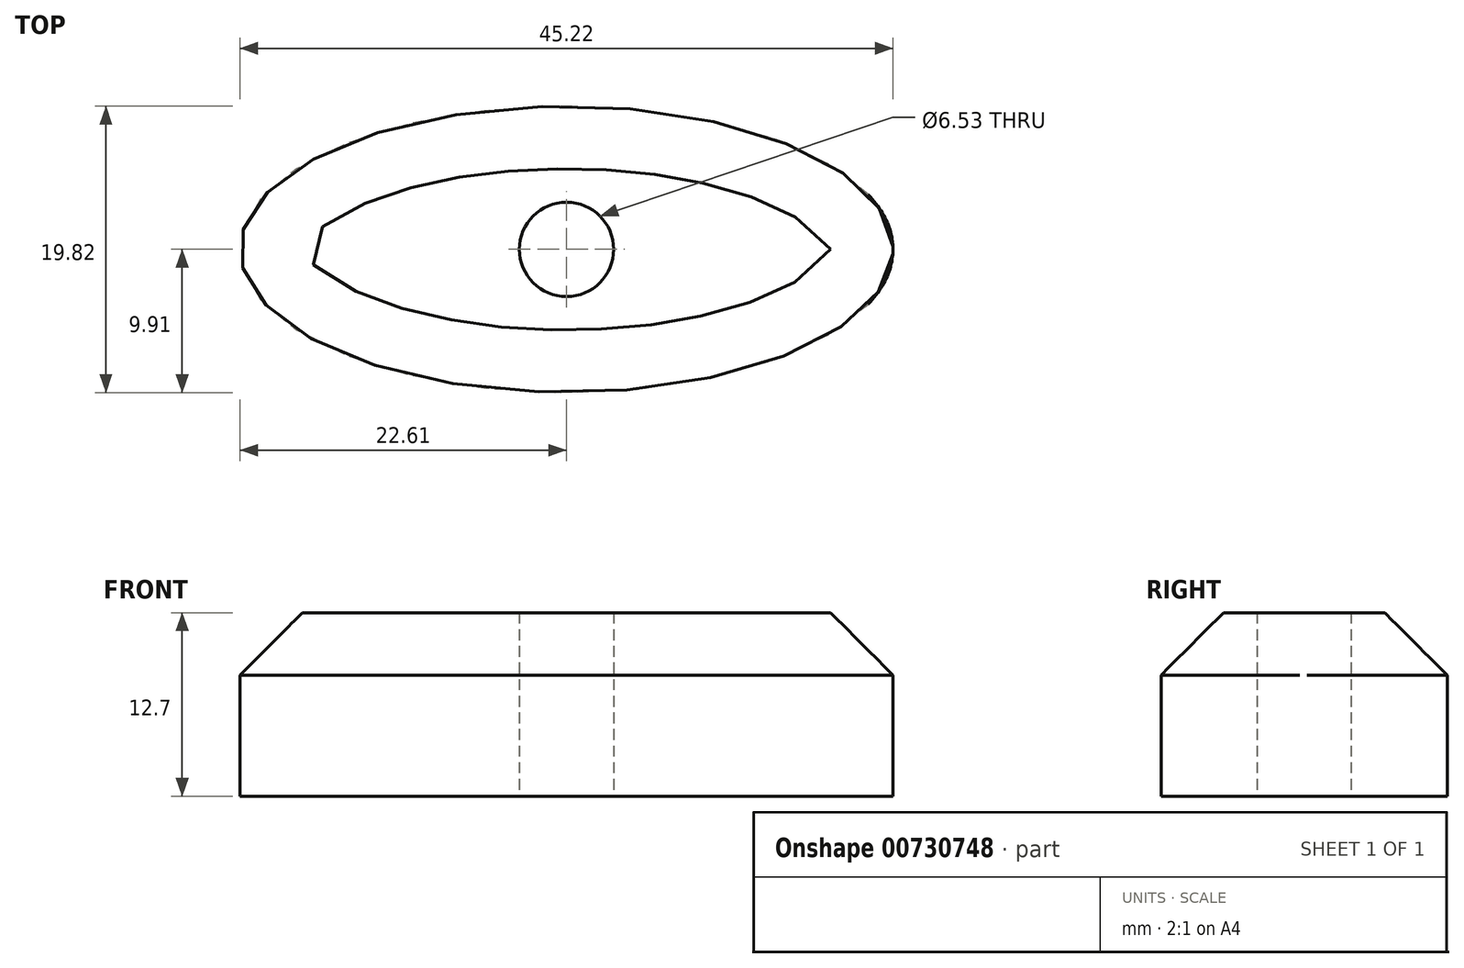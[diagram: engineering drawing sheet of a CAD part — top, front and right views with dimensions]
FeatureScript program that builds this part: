
annotation { "Feature Type Name" : "Feature", "Feature Type Description" : "" }
export const myFeature = defineFeature(function(context is Context, id is Id, definition is map)
    precondition{}
    {
        {
            var Q0;
            Q0=qCreatedBy(makeId("Top.planeOp"),FACE);
            var sketch = newSketch(context, id + "F0", { "sketchPlane" : qUnion([Q0])});
            skEllipse(sketch, "E0", {"center": v(0, 0) * mm, "majorRadius": 22.6 * mm, "minorRadius": 9.9 * mm, "majorAxis": v(1, 0)});
            skSolve(sketch);
        }
        {
            var Q0;
            Q0=makeQuery(id+"F0.imprint","IMPRINT",FACE,{"disambiguationData":[TD([[makeQuery(id+"F0.imprint","IMPRINT",EDGE,{"derivedFrom":sQuery(id+"F0.wireOp",EDGE,"E0")}),1.0]])]});
            extrude(context, id + "F1", {"entities" : qUnion([Q0]), "depth" : 12.7 * mm, "offsetDistance" : 25.4 * mm});
        }
        {
            var Q0;
            Q0=makeQuery(id+"F1.opExtrude","CAP_EDGE",EDGE,{"disambiguationData":[OSD([sQuery(id+"F0.wireOp",EDGE,"E0")])],"isStart":false});
            chamfer(context, id + "F2", {"entities" : qUnion([Q0]), "width" : 4.32 * mm, "tangentPropagation" : true});
        }
        {
            var Q0;
            Q0=makeQuery(id+"F1.opExtrude","CAP_FACE",FACE,{"disambiguationData":[OSD([sQuery(id+"F0.wireOp",EDGE,"E0")])],"isStart":true});
            var sketch = newSketch(context, id + "F3", { "sketchPlane" : qUnion([Q0])});
            skCircle(sketch, "E1", {"center": v(0, 0) * mm, "radius": 3.26 * mm});
            skSolve(sketch);
        }
        {
            var Q0;
            Q0=makeQuery(id+"F3.imprint","IMPRINT",FACE,{"disambiguationData":[TD([[makeQuery(id+"F3.imprint","IMPRINT",EDGE,{"derivedFrom":sQuery(id+"F3.wireOp",EDGE,"E1")}),1.0]])]});
            var Q1;
            Q1=sQuery(id+"F3.wireOp",EDGE,"E1");
            extrude(context, id + "F4", {"entities" : qUnion([Q0]), "operationType" : NewBodyOperationType.REMOVE, "surfaceEntities" : qUnion([Q1]), "endBound" : BoundingType.UP_TO_NEXT, "oppositeDirection" : true, "depth" : 25.4 * mm, "offsetDistance" : 25.4 * mm});
        }
    });
